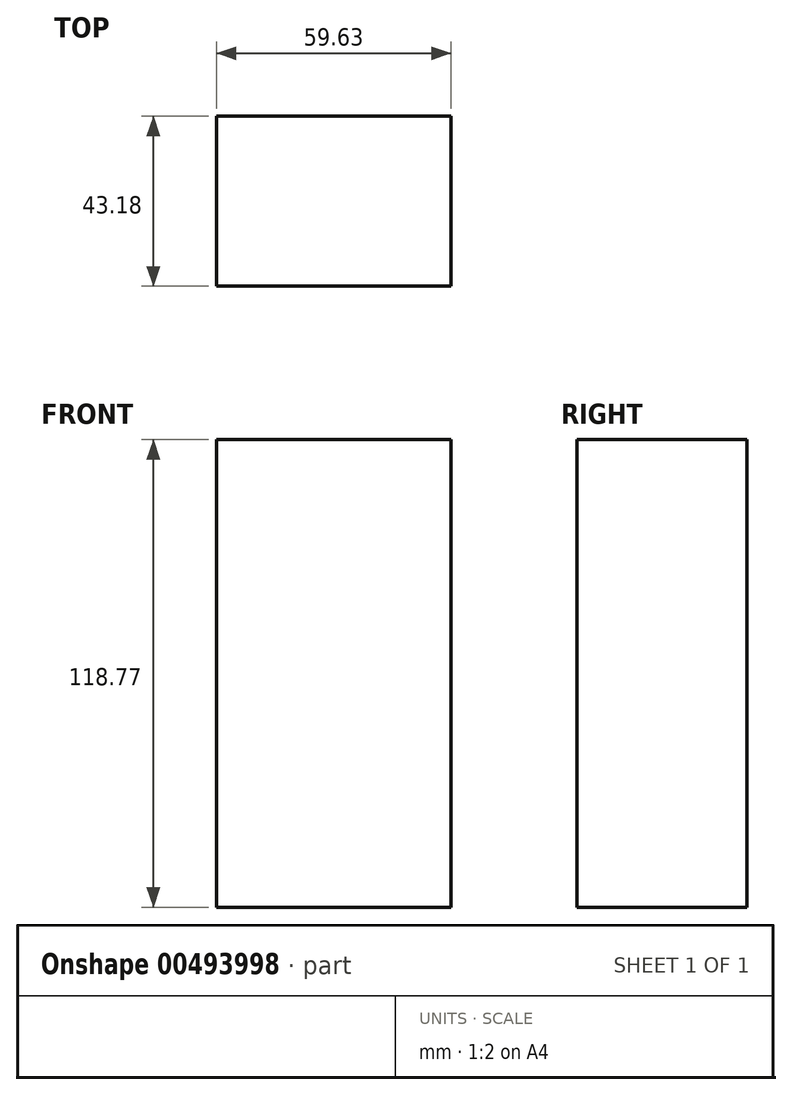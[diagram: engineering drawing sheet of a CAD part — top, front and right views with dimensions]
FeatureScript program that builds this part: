
annotation { "Feature Type Name" : "Feature", "Feature Type Description" : "" }
export const myFeature = defineFeature(function(context is Context, id is Id, definition is map)
    precondition{}
    {
        {
            var Q0;
            Q0=qCreatedBy(makeId("Front.planeOp"),FACE);
            var sketch = newSketch(context, id + "F0", { "sketchPlane" : qUnion([Q0])});
            skLineSegment(sketch, "E0", {"start": v(-31.28, 54.2) * mm, "end": v(-31.28, -56.73) * mm});
            skLineSegment(sketch, "E1", {"start": v(-31.28, -56.73) * mm, "end": v(28.35, -56.73) * mm});
            skLineSegment(sketch, "E2", {"start": v(28.35, -56.73) * mm, "end": v(28.35, 54.2) * mm});
            skLineSegment(sketch, "E3", {"start": v(-22.01, 62.04) * mm, "end": v(28.35, 62.04) * mm});
            skLineSegment(sketch, "E4", {"start": v(28.35, 54.2) * mm, "end": v(28.35, 62.04) * mm});
            skLineSegment(sketch, "E5", {"start": v(-22.01, 62.04) * mm, "end": v(-31.28, 62.04) * mm});
            skLineSegment(sketch, "E6", {"start": v(-31.28, 54.2) * mm, "end": v(-31.28, 62.04) * mm});
            skSolve(sketch);
        }
        {
            var Q0;
            Q0=makeQuery(id+"F0.imprint","IMPRINT",FACE,{"disambiguationData":[TD([[makeQuery(id+"F0.imprint","IMPRINT",EDGE,{"derivedFrom":sQuery(id+"F0.wireOp",EDGE,"E0")}),1.0]])]});
            extrude(context, id + "F1", {"entities" : qUnion([Q0]), "depth" : 43.18 * mm});
        }
    });
